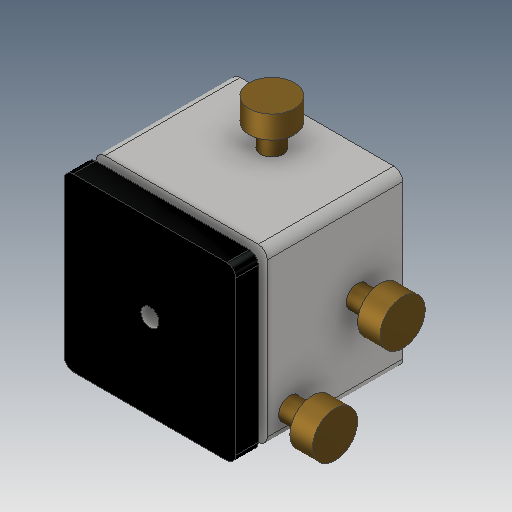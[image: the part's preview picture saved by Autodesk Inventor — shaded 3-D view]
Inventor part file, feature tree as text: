
AUTODESK INVENTOR PART (.ipt)
format: ipt  version: 2019 (Build 230136000, 136)  size: 190,464 bytes
history: native  units: mm
features: extrude x8, sketch x8, fillet x1, projected_geometry x1
ambient origin geometry x8: Origin, YZ Plane, XZ Plane, XY Plane, X Axis, Y Axis, Z Axis, Center Point
bodies: Solid1 (feature_tree)
feature tree (18):
  extrude  "Extrusion1"  Depth=38.0mm
  extrude  "Extrusion2"  Depth=5.0mm
  extrude  "Extrusion3"  Depth=5.0mm TaperAngle=0.0deg
  extrude  "Extrusion4"  Depth=5.0mm TaperAngle=0.0deg
  extrude  "Extrusion5"  Depth=5.0mm TaperAngle=0.0deg
  extrude  "Extrusion6"  Depth=5.0mm
  extrude  "Extrusion7"  Depth=10.0mm
  fillet  "Fillet1"  Radius=10.0mm
  extrude  "Extrusion8"  Depth=2.0mm
  sketch  "Sketch1"  dims[d0=38.0mm d1=38.0mm]
  sketch  "Sketch2"  dims[d2=30.0mm d3=0.0mm d4=5.0mm]
  sketch  "Sketch3"  dims[d5=2.0mm d6=0.0mm d7=5.0mm d8=0.0mm]
  sketch  "Sketch4"  dims[d9=5.0mm d10=5.0mm d11=0.0mm]
  sketch  "Sketch5"  dims[d12=10.0mm d13=5.0mm d14=0.0mm]
  sketch  "Sketch6"  dims[d15=5.0mm d16=5.0mm]
  sketch  "Sketch7"  dims[d17=5.0mm d18=0.0mm d19=10.0mm d20=10.0mm]
  projected_geometry  "Projected Loop1"
  sketch  "Sketch8"  dims[d21=5.0mm d22=0.0mm d23=2.0mm d24=4.0mm d25=5.0mm d26=0.0mm]
